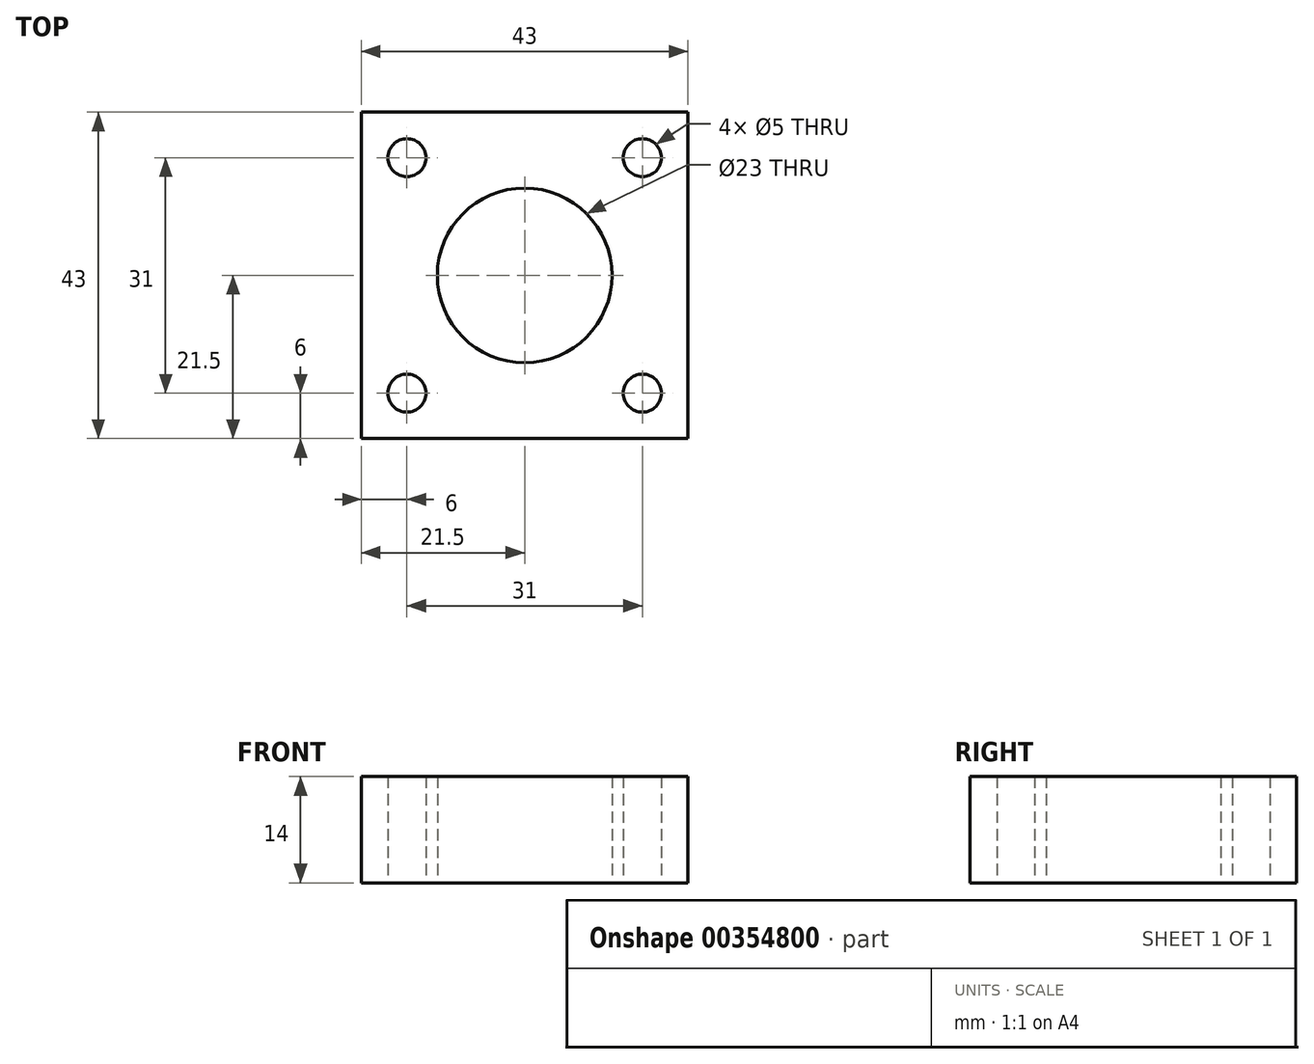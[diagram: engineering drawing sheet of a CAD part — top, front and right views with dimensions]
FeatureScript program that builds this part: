
annotation { "Feature Type Name" : "Feature", "Feature Type Description" : "" }
export const myFeature = defineFeature(function(context is Context, id is Id, definition is map)
    precondition{}
    {
        {
            var Q0;
            Q0=qCreatedBy(makeId("Top.planeOp"),FACE);
            var sketch = newSketch(context, id + "F0", { "sketchPlane" : qUnion([Q0])});
            skLineSegment(sketch, "E0.bottom", {"start": v(15.5, -15.5) * mm, "end": v(-15.5, -15.5) * mm, "construction": true});
            skLineSegment(sketch, "E0.top", {"start": v(15.5, 15.5) * mm, "end": v(-15.5, 15.5) * mm, "construction": true});
            skLineSegment(sketch, "E0.left", {"start": v(15.5, -15.5) * mm, "end": v(15.5, 15.5) * mm, "construction": true});
            skLineSegment(sketch, "E0.right", {"start": v(-15.5, -15.5) * mm, "end": v(-15.5, 15.5) * mm, "construction": true});
            skPoint(sketch, "E0.middle", {"position": v(0, 0) * mm});
            skCircle(sketch, "E1", {"center": v(15.5, 15.5) * mm, "radius": 2.5 * mm});
            skCircle(sketch, "E2", {"center": v(15.5, -15.5) * mm, "radius": 2.5 * mm});
            skCircle(sketch, "E3", {"center": v(-15.5, -15.5) * mm, "radius": 2.5 * mm});
            skCircle(sketch, "E4", {"center": v(-15.5, 15.5) * mm, "radius": 2.5 * mm});
            skCircle(sketch, "E5", {"center": v(0, 0) * mm, "radius": 11.5 * mm});
            skLineSegment(sketch, "E6.bottom", {"start": v(21.5, -21.5) * mm, "end": v(-21.5, -21.5) * mm});
            skLineSegment(sketch, "E6.top", {"start": v(21.5, 21.5) * mm, "end": v(-21.5, 21.5) * mm});
            skLineSegment(sketch, "E6.left", {"start": v(21.5, -21.5) * mm, "end": v(21.5, 21.5) * mm});
            skLineSegment(sketch, "E6.right", {"start": v(-21.5, -21.5) * mm, "end": v(-21.5, 21.5) * mm});
            skLineSegment(sketch, "E7.bottom", {"start": v(-21.5, 21.5) * mm, "end": v(-33.5, 21.5) * mm});
            skLineSegment(sketch, "E7.top", {"start": v(-21.5, 31.5) * mm, "end": v(-33.5, 31.5) * mm});
            skLineSegment(sketch, "E7.left", {"start": v(-21.5, 21.5) * mm, "end": v(-21.5, 31.5) * mm});
            skLineSegment(sketch, "E7.right", {"start": v(-33.5, 21.5) * mm, "end": v(-33.5, 31.5) * mm});
            skLineSegment(sketch, "E8.MirrorCS", {"start": v(21.5, 31.5) * mm, "end": v(33.5, 31.5) * mm});
            skLineSegment(sketch, "E9.MirrorCS", {"start": v(21.5, 21.5) * mm, "end": v(21.5, 31.5) * mm});
            skLineSegment(sketch, "E10.MirrorCS", {"start": v(21.5, 21.5) * mm, "end": v(33.5, 21.5) * mm});
            skLineSegment(sketch, "E11.MirrorCS", {"start": v(33.5, 21.5) * mm, "end": v(33.5, 31.5) * mm});
            skSolve(sketch);
        }
        {
            var Q0;
            Q0=makeQuery(id+"F0.imprint","IMPRINT",FACE,{"disambiguationData":[TD([[makeQuery(id+"F0.imprint","IMPRINT",EDGE,{"derivedFrom":sQuery(id+"F0.wireOp",EDGE,"E1")}),-1.0]])]});
            extrude(context, id + "F1", {"entities" : qUnion([Q0]), "depth" : 14 * mm});
        }
    });
